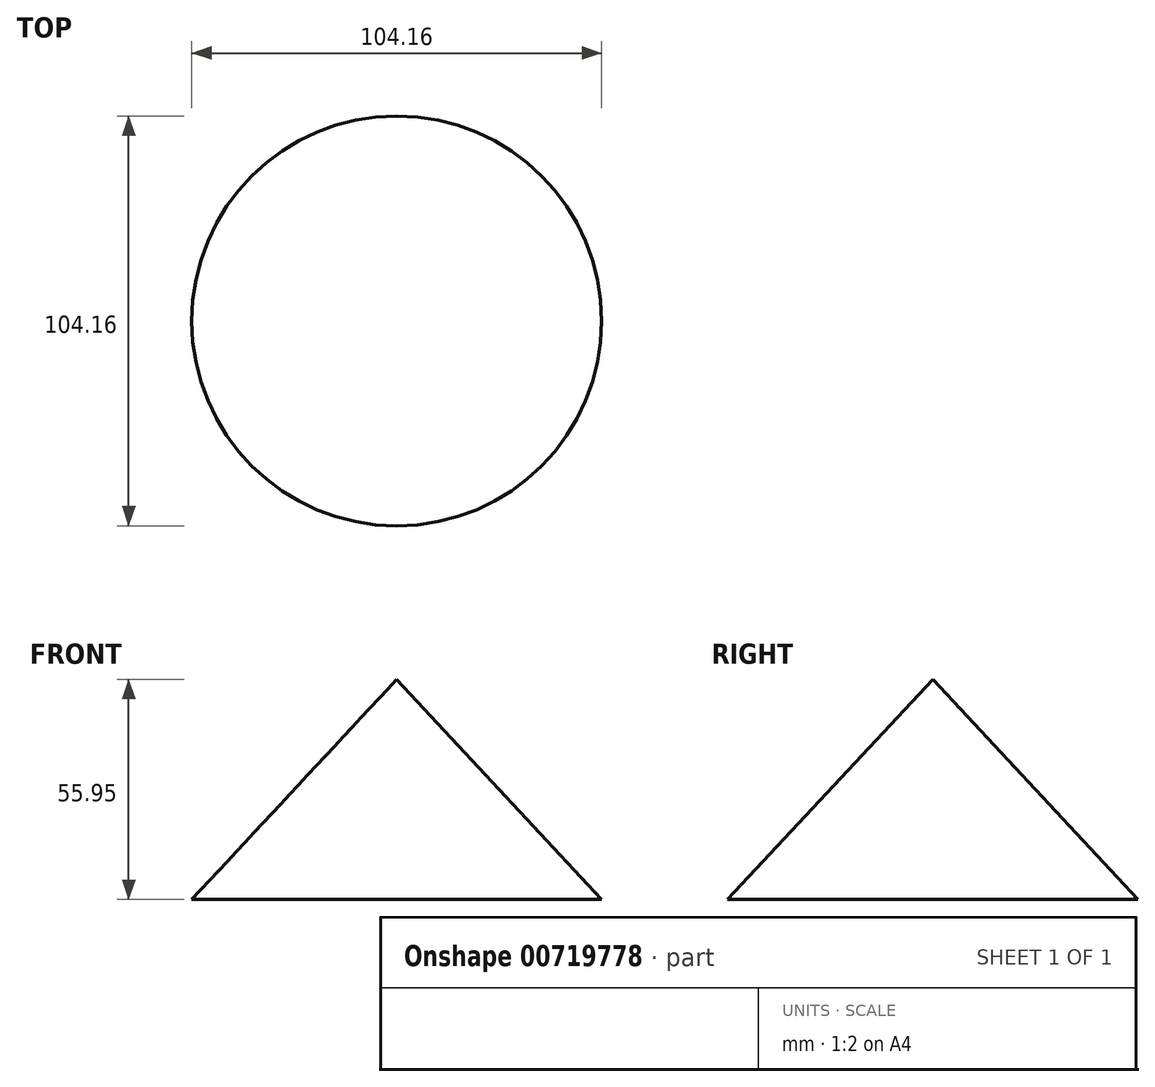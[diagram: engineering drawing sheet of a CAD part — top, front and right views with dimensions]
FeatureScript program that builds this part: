
annotation { "Feature Type Name" : "Feature", "Feature Type Description" : "" }
export const myFeature = defineFeature(function(context is Context, id is Id, definition is map)
    precondition{}
    {
        {
            var Q0;
            Q0=qCreatedBy(makeId("Right.planeOp"),FACE);
            var sketch = newSketch(context, id + "F0", { "sketchPlane" : qUnion([Q0])});
            skLineSegment(sketch, "E0", {"start": v(-52.08, 0) * mm, "end": v(0, 0) * mm});
            skLineSegment(sketch, "E1", {"start": v(0, 0) * mm, "end": v(0, 55.95) * mm});
            skLineSegment(sketch, "E2", {"start": v(0, 55.95) * mm, "end": v(-52.08, 0) * mm});
            skSolve(sketch);
        }
        {
            var Q0;
            Q0=sQuery(id+"F0.wireOp",EDGE,"E2");
            var Q1;
            Q1=sQuery(id+"F0.wireOp",EDGE,"E1");
            revolve(context, id + "F1", {"bodyType" : ToolBodyType.SURFACE, "surfaceOperationType" : NewSurfaceOperationType.NEW, "surfaceEntities" : qUnion([Q0]), "axis" : qUnion([Q1]), "revolveType" : RevolveType.FULL});
        }
    });
